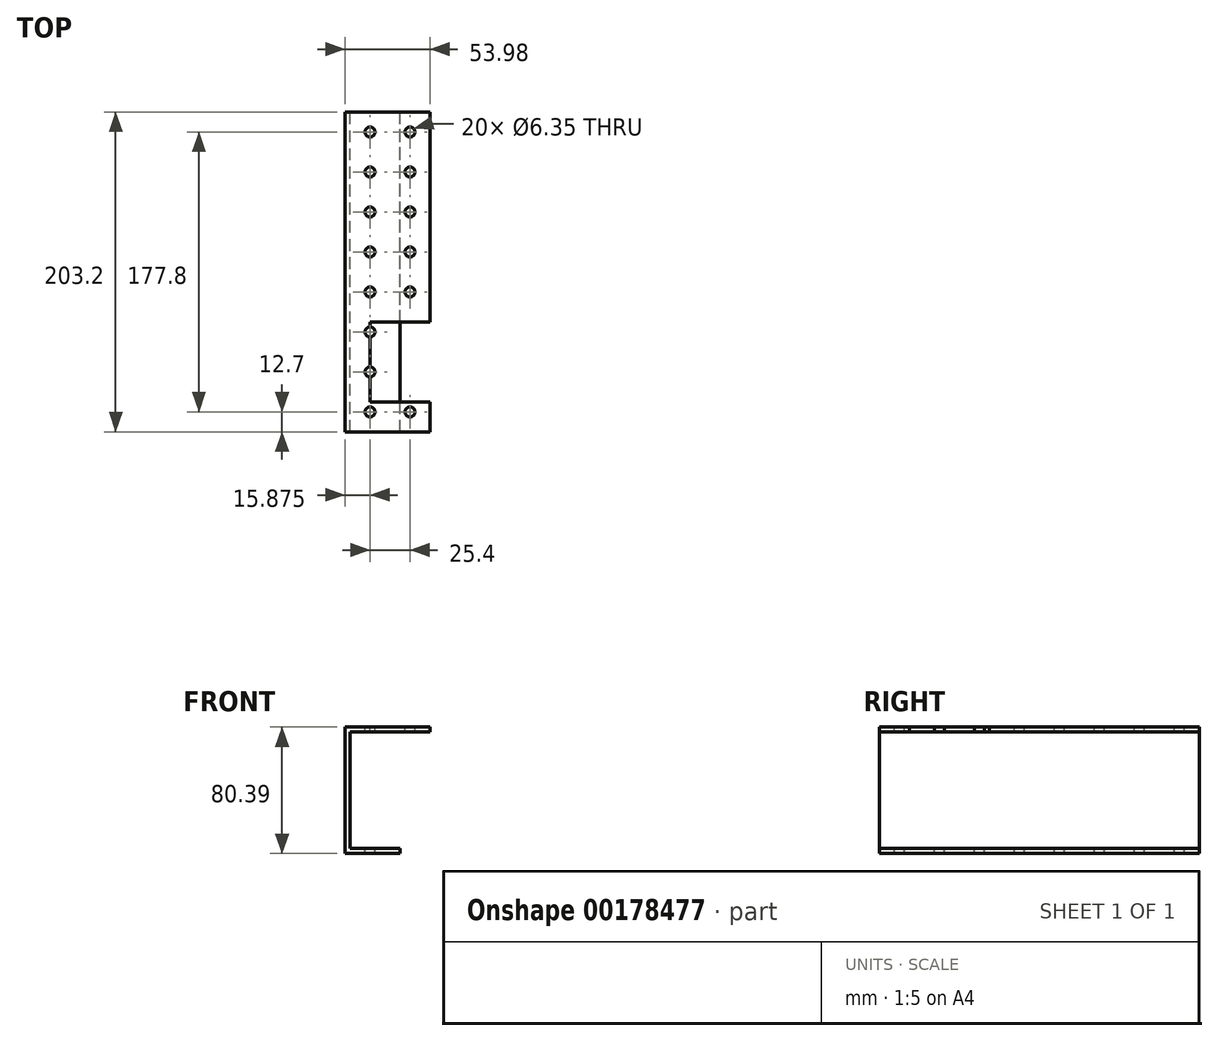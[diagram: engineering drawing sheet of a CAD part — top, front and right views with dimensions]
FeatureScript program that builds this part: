
annotation { "Feature Type Name" : "Feature", "Feature Type Description" : "" }
export const myFeature = defineFeature(function(context is Context, id is Id, definition is map)
    precondition{}
    {
        {
            var Q0;
            Q0=qCreatedBy(makeId("Front.planeOp"),FACE);
            var sketch = newSketch(context, id + "F0", { "sketchPlane" : qUnion([Q0])});
            skLineSegment(sketch, "E0", {"start": v(0, 44.52) * mm, "end": v(0, -35.87) * mm});
            skLineSegment(sketch, "E1", {"start": v(0, 44.52) * mm, "end": v(53.98, 44.52) * mm});
            skLineSegment(sketch, "E2", {"start": v(0, -35.87) * mm, "end": v(34.93, -35.87) * mm});
            skLineSegment(sketch, "E3", {"start": v(34.93, -35.87) * mm, "end": v(34.93, -32.7) * mm});
            skLineSegment(sketch, "E4", {"start": v(34.93, -32.7) * mm, "end": v(3.18, -32.7) * mm});
            skLineSegment(sketch, "E5", {"start": v(3.18, -32.7) * mm, "end": v(3.18, 41.34) * mm});
            skLineSegment(sketch, "E6", {"start": v(3.18, 41.34) * mm, "end": v(53.98, 41.34) * mm});
            skLineSegment(sketch, "E7", {"start": v(53.98, 41.34) * mm, "end": v(53.98, 44.52) * mm});
            skSolve(sketch);
        }
        {
            var Q0;
            Q0=makeQuery(id+"F0.imprint","IMPRINT",FACE,{"disambiguationData":[TD([[makeQuery(id+"F0.imprint","IMPRINT",EDGE,{"derivedFrom":sQuery(id+"F0.wireOp",EDGE,"E0")}),1.0]])]});
            extrude(context, id + "F1", {"entities" : qUnion([Q0]), "depth" : 203.2 * mm});
        }
        {
            var Q0;
            Q0=makeQuery(id+"F1.opExtrude","SWEPT_FACE",FACE,{"disambiguationData":[OSD([sQuery(id+"F0.wireOp",EDGE,"E1")])]});
            var sketch = newSketch(context, id + "F2", { "sketchPlane" : qUnion([Q0])});
            skCircle(sketch, "E8", {"center": v(41.27, -190.5) * mm, "radius": 3.18 * mm});
            skCircle(sketch, "E9.0.1.0", {"center": v(41.27, -165.1) * mm, "radius": 3.18 * mm});
            skCircle(sketch, "E9.0.2.0", {"center": v(41.27, -139.7) * mm, "radius": 3.18 * mm});
            skCircle(sketch, "E9.0.3.0", {"center": v(41.27, -114.3) * mm, "radius": 3.18 * mm});
            skCircle(sketch, "E9.0.4.0", {"center": v(41.27, -88.9) * mm, "radius": 3.18 * mm});
            skCircle(sketch, "E9.0.5.0", {"center": v(41.27, -63.5) * mm, "radius": 3.18 * mm});
            skCircle(sketch, "E9.0.6.0", {"center": v(41.27, -38.1) * mm, "radius": 3.18 * mm});
            skCircle(sketch, "E9.0.7.0", {"center": v(41.27, -12.7) * mm, "radius": 3.18 * mm});
            skCircle(sketch, "E9.1.0.0", {"center": v(15.87, -190.5) * mm, "radius": 3.18 * mm});
            skCircle(sketch, "E9.1.1.0", {"center": v(15.87, -165.1) * mm, "radius": 3.18 * mm});
            skCircle(sketch, "E9.1.2.0", {"center": v(15.87, -139.7) * mm, "radius": 3.18 * mm});
            skCircle(sketch, "E9.1.3.0", {"center": v(15.87, -114.3) * mm, "radius": 3.18 * mm});
            skCircle(sketch, "E9.1.4.0", {"center": v(15.87, -88.9) * mm, "radius": 3.18 * mm});
            skCircle(sketch, "E9.1.5.0", {"center": v(15.87, -63.5) * mm, "radius": 3.18 * mm});
            skCircle(sketch, "E9.1.6.0", {"center": v(15.87, -38.1) * mm, "radius": 3.18 * mm});
            skCircle(sketch, "E9.1.7.0", {"center": v(15.87, -12.7) * mm, "radius": 3.18 * mm});
            skLineSegment(sketch, "E9.direction1", {"start": v(41.27, -190.5) * mm, "end": v(15.87, -190.5) * mm, "construction": true});
            skLineSegment(sketch, "E9.direction2", {"start": v(41.27, -190.5) * mm, "end": v(41.27, -165.1) * mm, "construction": true});
            skSolve(sketch);
        }
        {
            var Q0;
            Q0=qSketchRegion(id+"F2",true);
            extrude(context, id + "F3", {"entities" : qUnion([Q0]), "operationType" : NewBodyOperationType.REMOVE, "oppositeDirection" : true, "depth" : 101.6 * mm});
        }
        {
            var Q0;
            Q0=makeQuery(id+"F1.opExtrude","SWEPT_FACE",FACE,{"disambiguationData":[OSD([sQuery(id+"F0.wireOp",EDGE,"E1")])]});
            var sketch = newSketch(context, id + "F4", { "sketchPlane" : qUnion([Q0])});
            skLineSegment(sketch, "E10", {"start": v(53.98, -184.15) * mm, "end": v(15.88, -184.15) * mm});
            skLineSegment(sketch, "E11", {"start": v(15.88, -184.15) * mm, "end": v(15.88, -133.35) * mm});
            skLineSegment(sketch, "E12", {"start": v(15.88, -133.35) * mm, "end": v(53.98, -133.35) * mm});
            skSolve(sketch);
        }
        {
            var Q0;
            {var subQ7=sQuery(id+"F4.wireOp",EDGE,"E10");Q0=makeQuery(id+"F4.imprint","IMPRINT",FACE,{"disambiguationData":[TD([[makeQuery(id+"F4.imprint","IMPRINT",EDGE,{"derivedFrom":subQ7}),-1.0]])]});}
            extrude(context, id + "F5", {"entities" : qUnion([Q0]), "operationType" : NewBodyOperationType.REMOVE, "oppositeDirection" : true, "depth" : 25.4 * mm});
        }
    });
